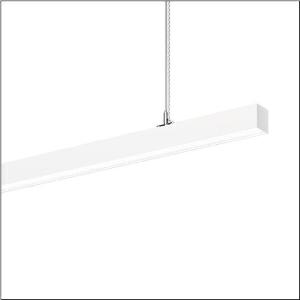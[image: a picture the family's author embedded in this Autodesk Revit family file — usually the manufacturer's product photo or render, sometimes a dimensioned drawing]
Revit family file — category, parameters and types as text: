
# Revit family: silica_r__21_51mx30da44wb_0345
name_source: partatom
category: Lighting Fixtures
units: mm (PartAtom-declared; Revit-internal decimal feet)

## family parameters
Cut with Voids When Loaded = No
Host = Face
Light Source = No
Part Type = Normal
Room Calculation Point = No
Round Connector Dimension = Use Diameter
Shared = No

## types (1)
- --- (1 x LED, 4210 lm, 26 W, 4000K)
    Apparent Load = 26 VA
    CIE Flux Codes = 47 79 96 57 100
    Color Rendering = 80
    Color Temperature = 4000K
    Default Elevation = 1800 mm
    Description = Silica® 21, office luminaire, primary optical cover: cover, of PMMA, opal, light emission: direct/indirect distribution, primary light characteristic: symmetric, installation type: suspended mounting, LED, rated luminous flux: 4.210lm, luminous efficacy: 162lm/W, light colour: 840, colour temperature: 4000K, with terminal, 3+2-pole, max. 2.5mm², mains connection: 220..240V, AC, 50/60Hz, rated input power: 26W, luminaire housing, of aluminium, traffic white (RAL 9016), length: 1.204mm, width: 53mm, height: 53mm, protection rating (complete): IP20, insulation class (complete): insulation class I (protective earthing), certification: CE, permissible operating ambient temperature: 0..+35°C, standard: EN 50419, packaging unit: 1 piece
    Height = 53 mm
    Lamp = 1 x LED
    Lamp Light Flux = 4210 lm
    Lamp Power = 26 W
    Lamp count = 1
    Length = 1204 mm
    Luminous efficacy = 162 lm/W
    Manufacturer = Siteco
    ModVariant = No
    Model = 51MX30DA44WB
    Mounting Place = Ceiling
    Mounting Type = Pendant
    Number of Poles = 1
    OnlyDefault = Yes
    Power Factor = 1
    Product Name = Silica® 21
    Product group = office luminaire | ceiling pendant
    ProductGroupID = 902
    Protection Class = Protection class I
    Protection Degree = IP 20
    RLX_Detail_Level = 1
    RLX_Emergency_Light_Flux = 0 lm
    RLX_Emergency_Type = 0
    RLX_Emergency_Type_DB = No
    RlxData = <blob elided: 21137 chars, md5=a625fc8b>
    Socket = socket
    Standby Power = 0 W
    System Light Flux = 4210 lm
    System Power = 26 W
    Type Comments = factory setting: luminous flux: 100 % | dim-lin: 254 | 218 mA
    Type Image = l_1313629.jpg
    URL = http://relux.com
    VarID = @adj_065711
    Voltage = 0 V
    Weight = 0.00 kg
    Width = 53 mm

## geometry (parser evidence)
native form markers: Blend x4, Sweep x14
no freeform markers — native parametric forms only
